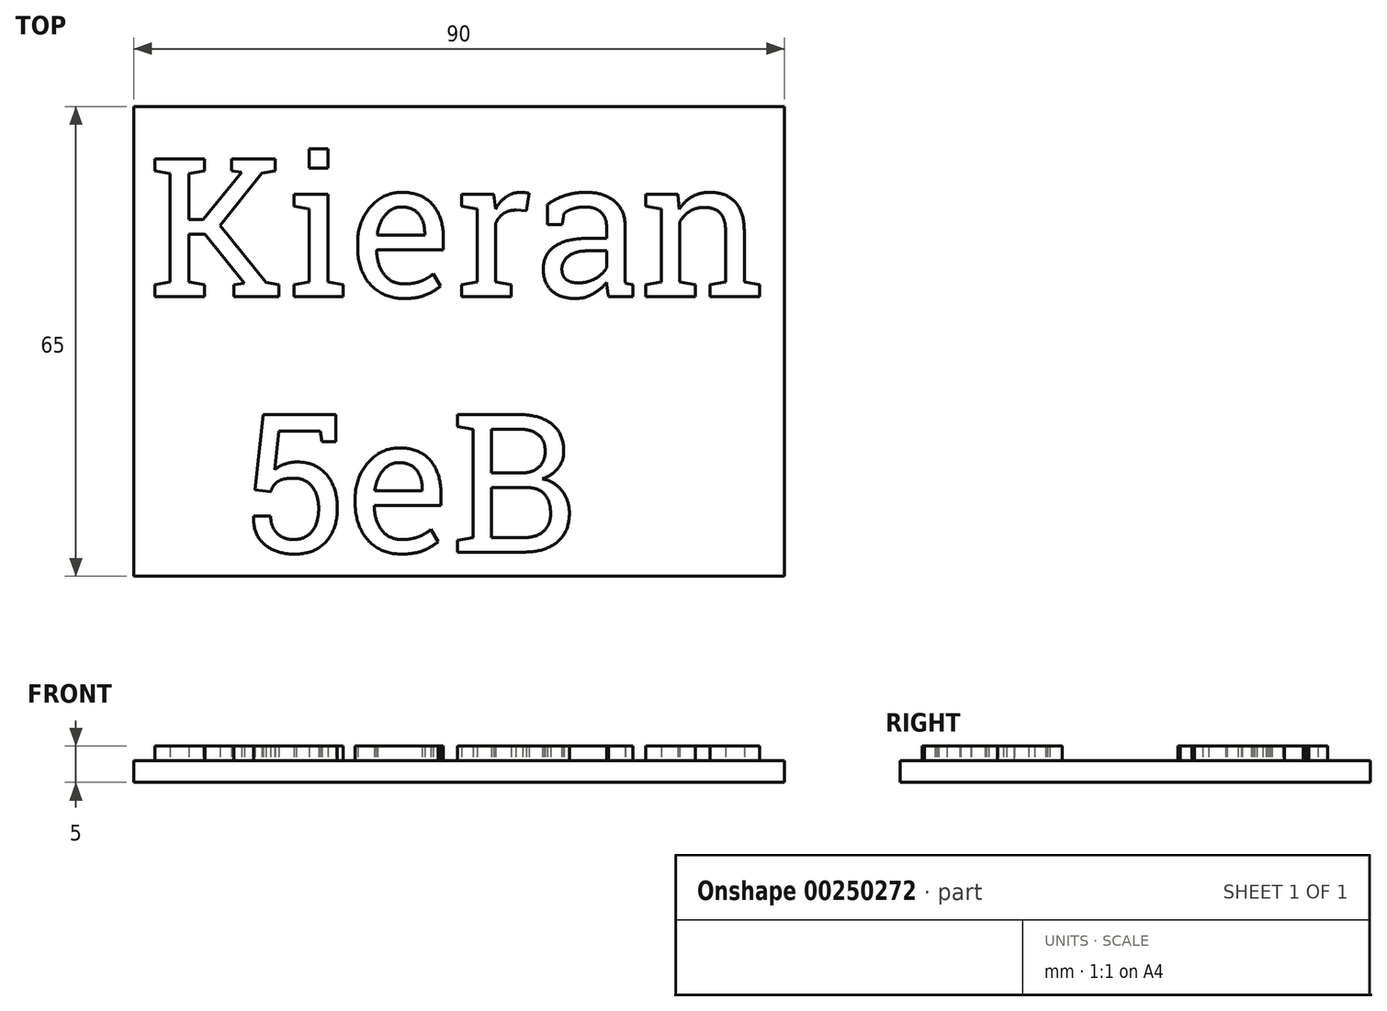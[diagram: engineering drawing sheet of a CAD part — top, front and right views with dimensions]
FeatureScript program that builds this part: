
annotation { "Feature Type Name" : "Feature", "Feature Type Description" : "" }
export const myFeature = defineFeature(function(context is Context, id is Id, definition is map)
    precondition{}
    {
        {
            var Q0;
            Q0=qCreatedBy(makeId("Top.planeOp"),FACE);
            var sketch = newSketch(context, id + "F0", { "sketchPlane" : qUnion([Q0])});
            skLineSegment(sketch, "E0.bottom", {"start": v(0, 0) * mm, "end": v(90, 0) * mm});
            skLineSegment(sketch, "E0.top", {"start": v(0, -65) * mm, "end": v(90, -65) * mm});
            skLineSegment(sketch, "E0.left", {"start": v(0, 0) * mm, "end": v(0, -65) * mm});
            skLineSegment(sketch, "E0.right", {"start": v(90, 0) * mm, "end": v(90, -65) * mm});
            skSolve(sketch);
        }
        {
            var Q0;
            Q0=makeQuery(id+"F0.imprint","IMPRINT",FACE,{"disambiguationData":[TD([[makeQuery(id+"F0.imprint","IMPRINT",EDGE,{"derivedFrom":sQuery(id+"F0.wireOp",EDGE,"E0.bottom")}),-1.0]])]});
            extrude(context, id + "F1", {"entities" : qUnion([Q0]), "depth" : 3 * mm});
        }
        {
            var Q0;
            Q0=makeQuery(id+"F1.opExtrude","CAP_FACE",FACE,{"disambiguationData":[OSD([sQuery(id+"F0.wireOp",EDGE,"E0.bottom"),sQuery(id+"F0.wireOp",EDGE,"E0.top"),sQuery(id+"F0.wireOp",EDGE,"E0.left"),sQuery(id+"F0.wireOp",EDGE,"E0.right")])],"isStart":false});
            var sketch = newSketch(context, id + "F2", { "sketchPlane" : qUnion([Q0])});
            skText(sketch, "E1", { "text": "Kieran\n  5eB", "fontName": "RobotoSlab-Regular.ttf"});
            const initialGuessF2  = {"E1": [0.002, -0.02629, 1, 0, 0.01929]};
            skSetInitialGuess(sketch, initialGuessF2);
            skSolve(sketch);
        }
        {
            var Q0;
            Q0 = qSketchRegion(id + "F2", true);
            extrude(context, id + "F3", {"entities" : qUnion([Q0]), "operationType" : NewBodyOperationType.ADD, "depth" : 2 * mm});
        }
    });
